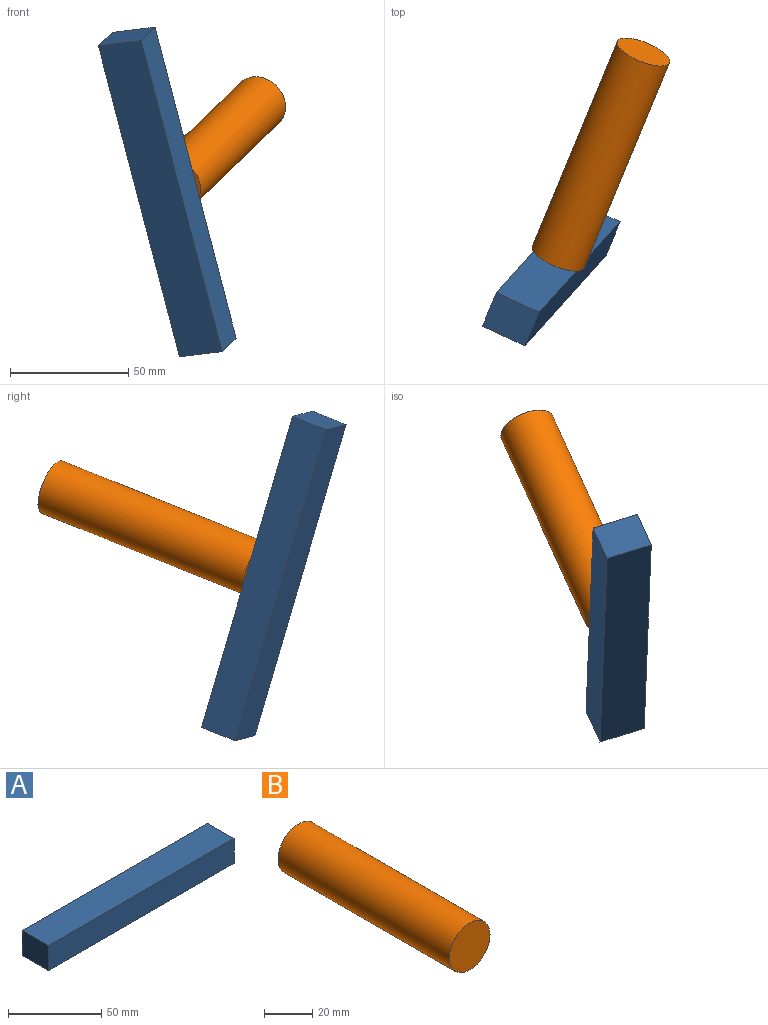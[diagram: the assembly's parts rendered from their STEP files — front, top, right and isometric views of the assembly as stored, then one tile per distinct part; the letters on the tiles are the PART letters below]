
ASSEMBLY  parts=2 mates=1
PART A: 6 faces, bbox 141.1x20x16.4 mm
  f0: plane 141.09x20mm, normal (0,0,-1), area 2821.8mm2, adj f1,f3,f4,f5
  f1: plane 20x16.41mm, normal (1,0,0), area 328.2mm2, adj f0,f2,f4,f5
  f2: plane 141.09x20mm, normal (0,0,1), area 2821.8mm2, adj f1,f3,f4,f5
  f3: plane 20x16.41mm, normal (-1,0,0), area 328.2mm2, adj f0,f2,f4,f5
  f4: plane 141.09x16.41mm, normal (0,-1,0), area 2315.3mm2, adj f0,f1,f2,f3
  f5: plane 141.09x16.41mm, normal (0,1,0), area 2315.3mm2, adj f0,f1,f2,f3
PART B: 3 faces, bbox 23.7x100x23.7 mm
  f0: cylinder r=11.86mm len=100mm, axis (0,-1,0), area 7453.5mm2, adj f1,f2
  f1: plane 23.73x23.73mm, normal (0,-1,0), area 442.1mm2, adj f0
  f2: plane 23.73x23.73mm, normal (0,1,0), area 442.1mm2, adj f0
PLACE A rot(axis=(0.46,-0.8,0.39),125.8deg) t=(-41.84,-93.32,78.92)mm
PLACE B rot(axis=(0.66,0.61,-0.45),38.1deg) t=(-30.92,-66.93,89.8)mm fixed
MATE revolute A.f0 <-> B.f0  axis (0.36,0.87,0.35) through (-48.9,-110.23,72.44)mm
